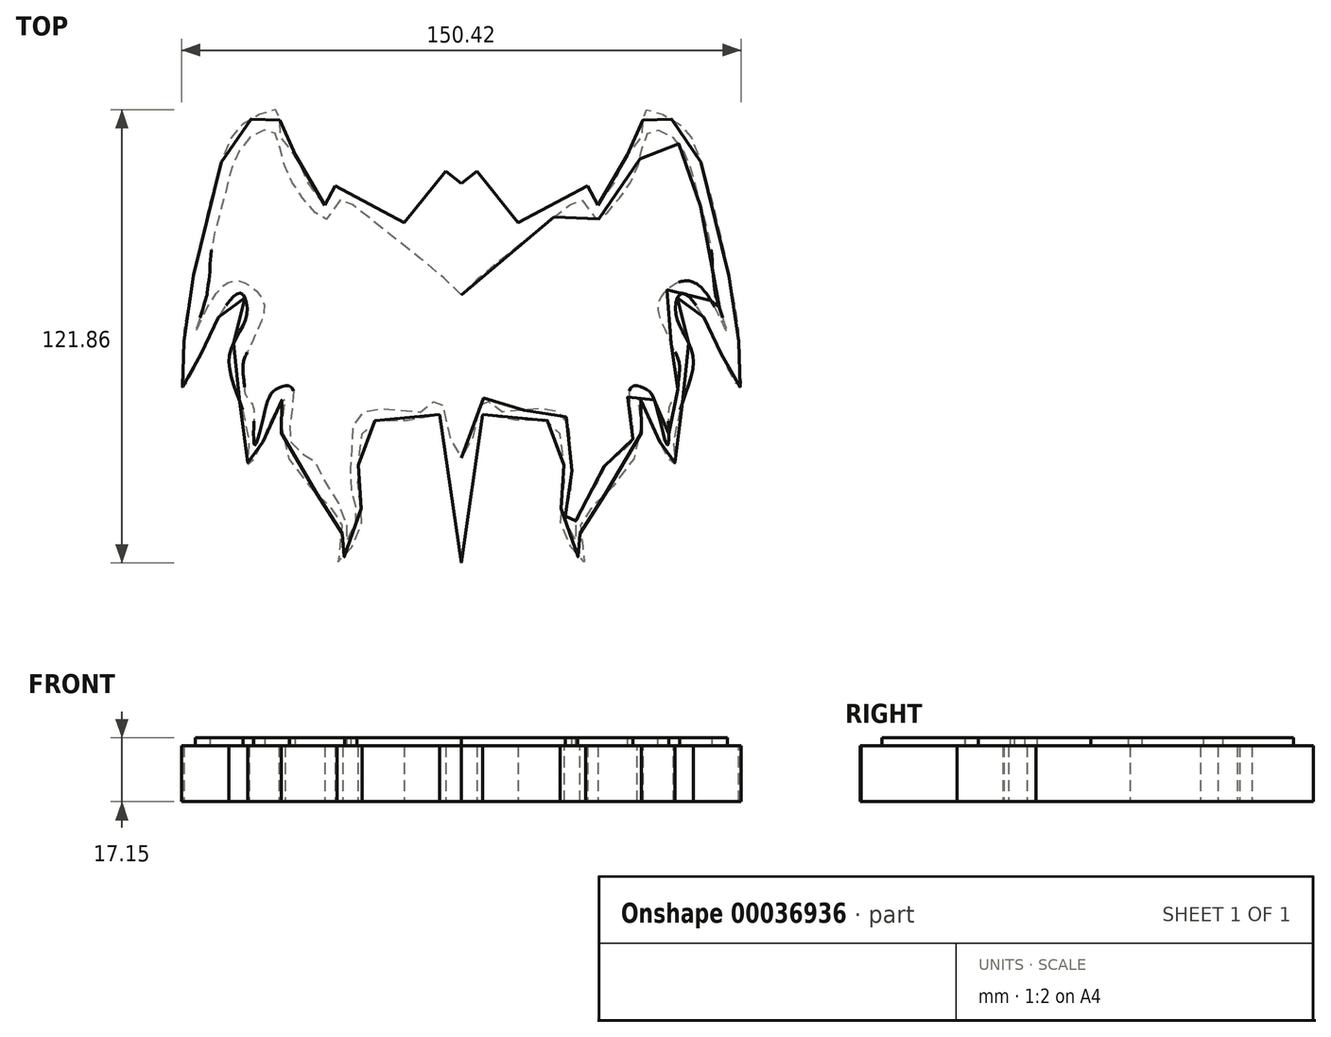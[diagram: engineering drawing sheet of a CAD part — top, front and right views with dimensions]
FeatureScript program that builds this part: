
annotation { "Feature Type Name" : "Feature", "Feature Type Description" : "" }
export const myFeature = defineFeature(function(context is Context, id is Id, definition is map)
    precondition{}
    {
        {
            var Q0;
            Q0=qCreatedBy(makeId("Top.planeOp"),FACE);
            var sketch = newSketch(context, id + "F0", { "sketchPlane" : qUnion([Q0])});
            skLineSegment(sketch, "E0", {"start": v(0, 29.95) * mm, "end": v(0, -72.02) * mm});
            skLineSegment(sketch, "E1", {"start": v(0, 29.95) * mm, "end": v(-4.16, 33.3) * mm});
            skLineSegment(sketch, "E2", {"start": v(-4.16, 33.3) * mm, "end": v(-15.27, 19.47) * mm});
            skLineSegment(sketch, "E3", {"start": v(-15.27, 19.47) * mm, "end": v(-15.27, 19.47) * mm});
            skLineSegment(sketch, "E4", {"start": v(-15.27, 19.47) * mm, "end": v(-33.92, 29.39) * mm});
            skLineSegment(sketch, "E5", {"start": v(-33.92, 29.39) * mm, "end": v(-36.68, 24.2) * mm});
            skLineSegment(sketch, "E6", {"start": v(0, -72.02) * mm, "end": v(-5.79, -32.08) * mm});
            skFitSpline(sketch, "E7", {"points": [v(-36.68, 24.2) * mm, v(-44.59, 37.6) * mm, v(-48.83, 43.3) * mm, v(-49.17, 49.55) * mm, v(-56.82, 47.11) * mm, v(-63.41, 38.77) * mm, v(-74.49, -9.5) * mm, v(-74.55, -14.02) * mm, v(-74.9, -24.75) * mm, v(-71.4, -19.17) * mm, v(-68.77, -13.22) * mm, v(-64.73, -5.2) * mm, v(-59.26, 0.5) * mm, v(-57.74, -5.68) * mm, v(-62.4, -17.15) * mm, v(-57.18, -37.3) * mm, v(-57.23, -45.95) * mm, v(-54.06, -41.11) * mm, v(-51.76, -35.3) * mm, v(-47.38, -27.15) * mm, v(-48.15, -39.03) * mm, v(-35.27, -56.93) * mm, v(-31.95, -64.25) * mm, v(-33.22, -71.67) * mm, v(-27.28, -63.67) * mm, v(-27.44, -54.3) * mm, v(-27.56, -44.95) * mm, v(-24.21, -34.15) * mm, v(-5.79, -32.08) * mm, v(0, 0) * mm, v(-36.68, 24.2) * mm]});
            skLineSegment(sketch, "E8.MirrorCS", {"start": v(0, 29.95) * mm, "end": v(4.16, 33.3) * mm});
            skLineSegment(sketch, "E9.MirrorCS", {"start": v(33.92, 29.39) * mm, "end": v(36.68, 24.2) * mm});
            skLineSegment(sketch, "E10.MirrorCS", {"start": v(15.27, 19.47) * mm, "end": v(15.27, 19.47) * mm});
            skLineSegment(sketch, "E11.MirrorCS", {"start": v(15.27, 19.47) * mm, "end": v(33.92, 29.39) * mm});
            skLineSegment(sketch, "E12.MirrorCS", {"start": v(4.16, 33.3) * mm, "end": v(15.27, 19.47) * mm});
            skFitSpline(sketch, "E13.MirrorC", {"points": [v(36.68, 24.2) * mm, v(44.59, 37.6) * mm, v(48.83, 43.3) * mm, v(49.17, 49.55) * mm, v(56.82, 47.11) * mm, v(63.41, 38.77) * mm, v(74.49, -9.5) * mm, v(74.55, -14.02) * mm, v(74.9, -24.75) * mm, v(71.4, -19.17) * mm, v(68.77, -13.22) * mm, v(64.73, -5.2) * mm, v(59.26, 0.5) * mm, v(57.74, -5.68) * mm, v(62.4, -17.15) * mm, v(57.18, -37.3) * mm, v(57.23, -45.95) * mm, v(54.06, -41.11) * mm, v(51.76, -35.3) * mm, v(47.38, -27.15) * mm, v(48.15, -39.03) * mm, v(35.27, -56.93) * mm, v(31.95, -64.25) * mm, v(33.22, -71.67) * mm, v(27.28, -63.67) * mm, v(27.44, -54.3) * mm, v(27.56, -44.95) * mm, v(24.21, -34.15) * mm, v(5.79, -32.08) * mm, v(0, 0) * mm, v(36.68, 24.2) * mm]});
            skLineSegment(sketch, "E14.MirrorCS", {"start": v(0, -72.02) * mm, "end": v(5.79, -32.08) * mm});
            skSolve(sketch);
        }
        {
            var Q0;
            {var subQ2=sQuery(id+"F0.wireOp",EDGE,"E7");var subQ5=makeQuery(id+"F0.imprint","INTERSECT",VERTEX,{"derivedFrom":[sQuery(id+"F0.wireOp",EDGE,"E5"),subQ2]});Q0=makeQuery(id+"F0.imprint","IMPRINT",FACE,{"disambiguationData":[TD([[makeQuery(id+"F0.imprint","IMPRINT",EDGE,{"disambiguationData":[TD([[subQ5,-1.0]])],"derivedFrom":subQ2}),1.0]])]});}
            var Q1;
            {var subQ0=sQuery(id+"F0.wireOp",EDGE,"E13.MirrorC");var subQ4=makeQuery(id+"F0.imprint","INTERSECT",VERTEX,{"derivedFrom":[sQuery(id+"F0.wireOp",EDGE,"E9.MirrorCS"),subQ0]});Q1=makeQuery(id+"F0.imprint","IMPRINT",FACE,{"disambiguationData":[TD([[makeQuery(id+"F0.imprint","IMPRINT",EDGE,{"disambiguationData":[TD([[subQ4,-1.0]])],"derivedFrom":subQ0}),-1.0]])]});}
            var Q2;
            {var subQ4=sQuery(id+"F0.wireOp",EDGE,"E1");Q2=makeQuery(id+"F0.imprint","IMPRINT",FACE,{"disambiguationData":[TD([[makeQuery(id+"F0.imprint","IMPRINT",EDGE,{"derivedFrom":subQ4}),1.0]])]});}
            var Q3;
            {var subQ4=sQuery(id+"F0.wireOp",EDGE,"E8.MirrorCS");Q3=makeQuery(id+"F0.imprint","IMPRINT",FACE,{"disambiguationData":[TD([[makeQuery(id+"F0.imprint","IMPRINT",EDGE,{"derivedFrom":subQ4}),-1.0]])]});}
            var Q4;
            {var subQ0=sQuery(id+"F0.wireOp",EDGE,"E13.MirrorC");var subQ1=sQuery(id+"F0.wireOp",EDGE,"E0");var subQ2=sQuery(id+"F0.wireOp",EDGE,"E7");var subQ4=makeQuery(id+"F0.imprint","INTERSECT",VERTEX,{"disambiguationData":[OD(0.0)],"derivedFrom":[subQ1,subQ2,subQ0]});Q4=makeQuery(id+"F0.imprint","IMPRINT",FACE,{"disambiguationData":[TD([[makeQuery(id+"F0.imprint","IMPRINT",EDGE,{"disambiguationData":[TD([[subQ4,-1.0]])],"derivedFrom":subQ1}),-1.0]])]});}
            var Q5;
            {var subQ0=sQuery(id+"F0.wireOp",EDGE,"E7");var subQ1=sQuery(id+"F0.wireOp",EDGE,"E0");var subQ2=sQuery(id+"F0.wireOp",EDGE,"E13.MirrorC");var subQ4=makeQuery(id+"F0.imprint","INTERSECT",VERTEX,{"disambiguationData":[OD(0.0)],"derivedFrom":[subQ1,subQ0,subQ2]});Q5=makeQuery(id+"F0.imprint","IMPRINT",FACE,{"disambiguationData":[TD([[makeQuery(id+"F0.imprint","IMPRINT",EDGE,{"disambiguationData":[TD([[subQ4,-1.0]])],"derivedFrom":subQ1}),1.0]])]});}
            var Q6;
            {var subQ3=sQuery(id+"F0.wireOp",EDGE,"E6");Q6=makeQuery(id+"F0.imprint","IMPRINT",FACE,{"disambiguationData":[TD([[makeQuery(id+"F0.imprint","IMPRINT",EDGE,{"derivedFrom":subQ3}),-1.0]])]});}
            var Q7;
            {var subQ0=sQuery(id+"F0.wireOp",EDGE,"E14.MirrorCS");Q7=makeQuery(id+"F0.imprint","IMPRINT",FACE,{"disambiguationData":[TD([[makeQuery(id+"F0.imprint","IMPRINT",EDGE,{"derivedFrom":subQ0}),1.0]])]});}
            extrude(context, id + "F1", {"entities" : qUnion([Q0, Q1, Q2, Q3, Q4, Q5, Q6, Q7]), "depth" : 15 * mm});
        }
        {
            var Q0;
            Q0=qCreatedBy(makeId("Top.planeOp"),FACE);
            var sketch = newSketch(context, id + "F2", { "sketchPlane" : qUnion([Q0])});
            skFitSpline(sketch, "E15", {"points": [v(-62.06, 32.76) * mm, v(-63.95, 25.2) * mm, v(-67.1, 12.6) * mm, v(-67.5, 7.23) * mm, v(-67.5, 7.22) * mm, v(-67.53, 6.57) * mm, v(-68.3, 0.33) * mm, v(-68.36, 0) * mm, v(-68.52, -0.59) * mm, v(-69.92, -5.15) * mm, v(-71.5, -10.08) * mm, v(-66.15, 0) * mm, v(-61.11, 3.78) * mm, v(-57.33, 2.83) * mm, v(-52.92, -2.52) * mm, v(-55.13, -10.08) * mm, v(-57.02, -14.5) * mm, v(-58.6, -18.27) * mm, v(-58.28, -24.26) * mm, v(-57.96, -26.78) * mm, v(-56.07, -29.61) * mm, v(-55.76, -34.97) * mm, v(-55.44, -40.32) * mm, v(-52.92, -31.82) * mm, v(-51.03, -26.46) * mm, v(-48.83, -24.89) * mm, v(-46, -24.57) * mm, v(-44.73, -28.67) * mm, v(-46, -32.13) * mm, v(-46, -36.23) * mm, v(-46, -39.38) * mm, v(-42.84, -42.53) * mm, v(-40.95, -43.47) * mm, v(-38.43, -46) * mm, v(-34.65, -54.18) * mm, v(-30.87, -59.54) * mm, v(-31.19, -66.15) * mm, v(-28.98, -63.32) * mm, v(-28.04, -58.9) * mm, v(-28.67, -55.76) * mm, v(-29.61, -51.66) * mm, v(-29.61, -45.36) * mm, v(-29.3, -40) * mm, v(-28.35, -33.08) * mm, v(-25.51, -31.19) * mm, v(-21.42, -30.56) * mm, v(-17.33, -30.87) * mm, v(-11.34, -31.5) * mm, v(-8.2, -29.61) * mm, v(-5.98, -27.72) * mm, v(-3.78, -35.6) * mm, v(0, -43.79) * mm, v(2.51, -35.33) * mm, v(3.2, -29.95) * mm, v(3.88, -22.06) * mm, v(4, -17.96) * mm, v(3.03, -7.27) * mm, v(0, 0) * mm, v(-23.63, 19.84) * mm, v(-33.08, 25.2) * mm, v(-35.91, 20.47) * mm, v(-41.9, 25.2) * mm, v(-47.88, 35.9) * mm, v(-50.72, 44.1) * mm, v(-57.33, 41.9) * mm, v(-62.06, 32.76) * mm]});
            skFitSpline(sketch, "E16.MirrorC", {"points": [v(62.06, 32.76) * mm, v(63.95, 25.2) * mm, v(67.1, 12.6) * mm, v(67.5, 7.23) * mm, v(67.5, 7.22) * mm, v(67.53, 6.57) * mm, v(68.3, 0.33) * mm, v(68.36, 0) * mm, v(68.52, -0.59) * mm, v(69.92, -5.15) * mm, v(71.5, -10.08) * mm, v(66.15, 0) * mm, v(61.11, 3.78) * mm, v(57.33, 2.83) * mm, v(52.92, -2.52) * mm, v(55.13, -10.08) * mm, v(57.02, -14.5) * mm, v(58.6, -18.27) * mm, v(58.28, -24.26) * mm, v(57.96, -26.78) * mm, v(56.07, -29.61) * mm, v(55.76, -34.97) * mm, v(55.44, -40.32) * mm, v(52.92, -31.82) * mm, v(51.03, -26.46) * mm, v(48.83, -24.89) * mm, v(46, -24.57) * mm, v(44.73, -28.67) * mm, v(46, -32.13) * mm, v(46, -36.23) * mm, v(46, -39.38) * mm, v(42.84, -42.53) * mm, v(40.95, -43.47) * mm, v(38.43, -46) * mm, v(34.65, -54.18) * mm, v(30.87, -59.54) * mm, v(31.19, -66.15) * mm, v(28.98, -63.32) * mm, v(28.04, -58.9) * mm, v(28.67, -55.76) * mm, v(29.61, -51.66) * mm, v(29.61, -45.36) * mm, v(29.3, -40) * mm, v(28.35, -33.08) * mm, v(25.51, -31.19) * mm, v(21.42, -30.56) * mm, v(17.33, -30.87) * mm, v(11.34, -31.5) * mm, v(8.2, -29.61) * mm, v(5.98, -27.72) * mm, v(3.78, -35.6) * mm, v(0, -43.79) * mm, v(-2.51, -35.33) * mm, v(-3.2, -29.95) * mm, v(-3.88, -22.06) * mm, v(-4, -17.96) * mm, v(-3.03, -7.27) * mm, v(0, 0) * mm, v(23.63, 19.84) * mm, v(33.08, 25.2) * mm, v(35.91, 20.47) * mm, v(41.9, 25.2) * mm, v(47.88, 35.9) * mm, v(50.72, 44.1) * mm, v(57.33, 41.9) * mm, v(62.06, 32.76) * mm]});
            skSolve(sketch);
        }
        {
            var Q0;
            Q0 = qSketchRegion(id + "F2", true);
            extrude(context, id + "F3", {"entities" : qUnion([Q0]), "operationType" : NewBodyOperationType.ADD, "depth" : 17.15 * mm});
        }
    });
